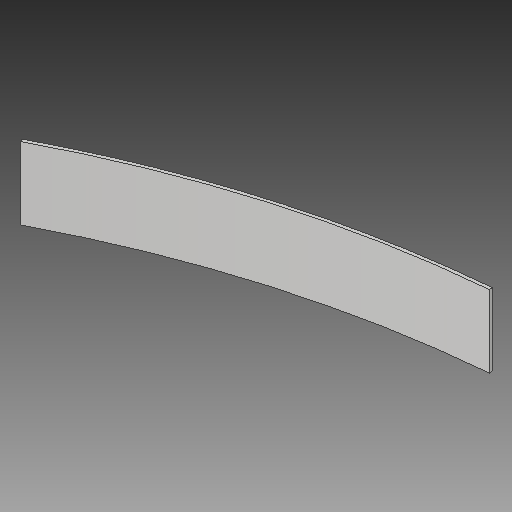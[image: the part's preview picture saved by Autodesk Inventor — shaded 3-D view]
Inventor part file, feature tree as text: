
AUTODESK INVENTOR PART (.ipt)
format: ipt  version: 2018 (Build 220112000, 112)  size: 134,144 bytes
history: native  units: mm
features: other x4, projected_geometry x2, extrude x1, sketch x1
ambient origin geometry x8: Origin, YZ Plane, XZ Plane, XY Plane, X Axis, Y Axis, Z Axis, Center Point
bodies: Body1 (feature_tree)
feature tree (8):
  other  "splitter.ipt"
  extrude  "押し出し2"  Depth=10.0mm
  other  "ソリッド162::splitter.ipt"
  other  "TaggingFeature1"
  sketch  "スケッチ2"
  projected_geometry  "投影ループ2"
  projected_geometry  "投影ループ3"
  other  "ソリッド1"
